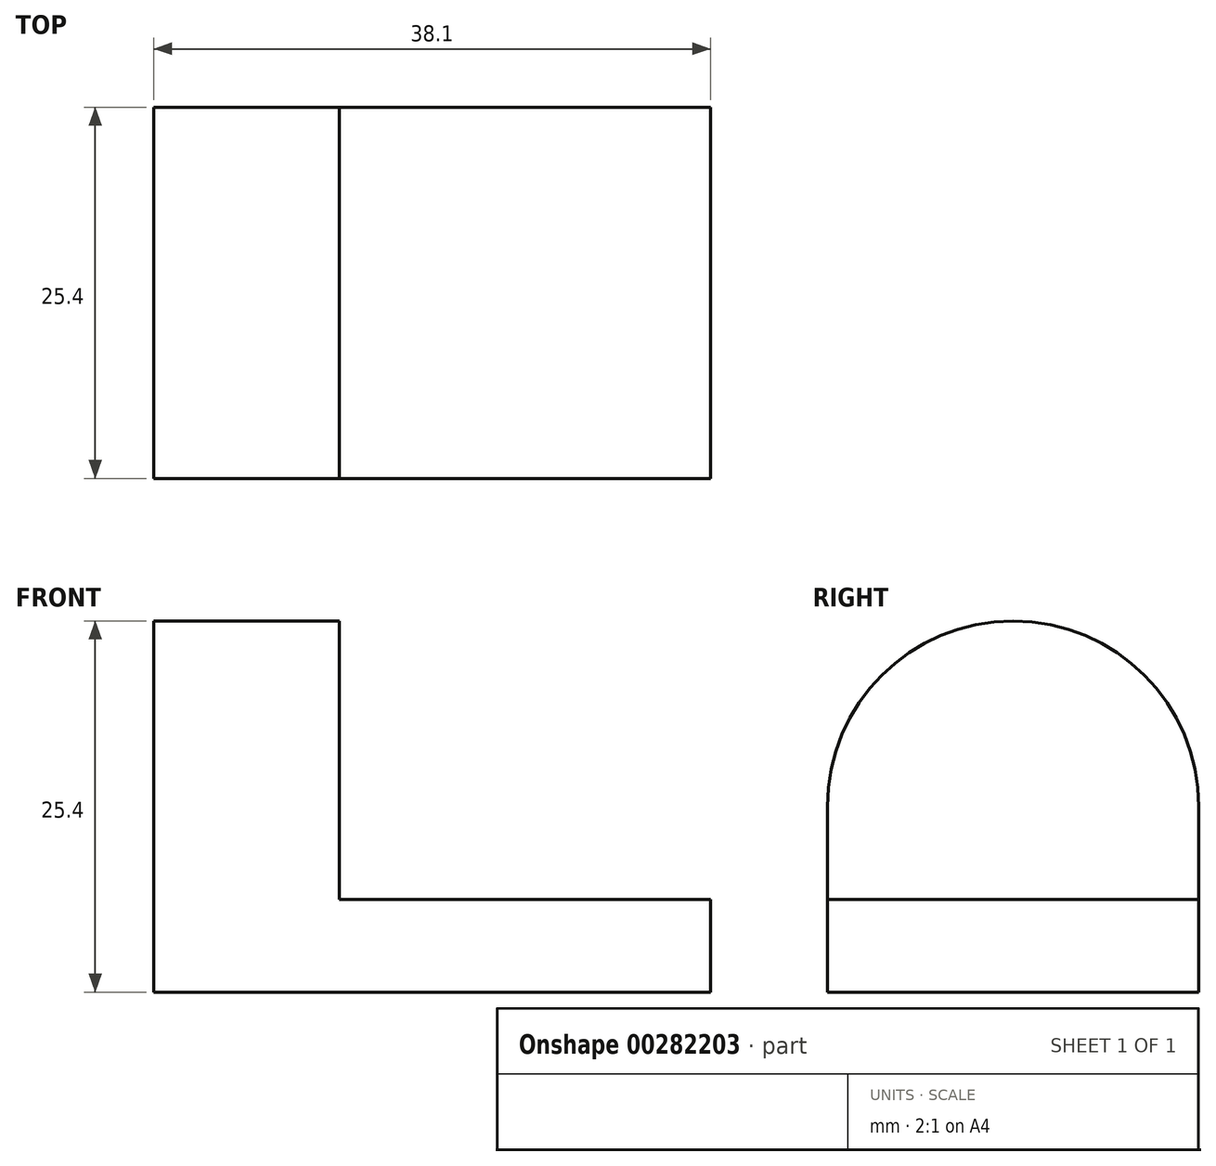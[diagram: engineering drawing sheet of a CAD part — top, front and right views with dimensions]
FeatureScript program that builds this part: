
annotation { "Feature Type Name" : "Feature", "Feature Type Description" : "" }
export const myFeature = defineFeature(function(context is Context, id is Id, definition is map)
    precondition{}
    {
        {
            var Q0;
            Q0=qCreatedBy(makeId("Right.planeOp"),FACE);
            var sketch = newSketch(context, id + "F0", { "sketchPlane" : qUnion([Q0])});
            skLineSegment(sketch, "E0.bottom", {"start": v(0, 0) * mm, "end": v(25.4, 0) * mm});
            skLineSegment(sketch, "E0.top", {"start": v(0, 6.35) * mm, "end": v(25.4, 6.35) * mm});
            skLineSegment(sketch, "E0.left", {"start": v(0, 0) * mm, "end": v(0, 6.35) * mm});
            skLineSegment(sketch, "E0.right", {"start": v(25.4, 0) * mm, "end": v(25.4, 6.35) * mm});
            skSolve(sketch);
        }
        {
            var Q0;
            Q0 = qSketchRegion(id + "F0", true);
            extrude(context, id + "F1", {"entities" : qUnion([Q0]), "depth" : 38.1 * mm});
        }
        {
            var Q0;
            Q0=qCreatedBy(makeId("Right.planeOp"),FACE);
            var sketch = newSketch(context, id + "F2", { "sketchPlane" : qUnion([Q0])});
            skLineSegment(sketch, "E1.bottom", {"start": v(25.4, 6.35) * mm, "end": v(0, 6.35) * mm});
            skLineSegment(sketch, "E1.top", {"start": v(25.4, 12.7) * mm, "end": v(0, 12.7) * mm});
            skLineSegment(sketch, "E1.left", {"start": v(25.4, 6.35) * mm, "end": v(25.4, 12.7) * mm});
            skLineSegment(sketch, "E1.right", {"start": v(0, 6.35) * mm, "end": v(0, 12.7) * mm});
            skSolve(sketch);
        }
        {
            var Q0;
            Q0 = qSketchRegion(id + "F2", true);
            extrude(context, id + "F3", {"entities" : qUnion([Q0]), "operationType" : NewBodyOperationType.ADD, "depth" : 12.7 * mm});
        }
        {
            var Q0;
            Q0=qCreatedBy(makeId("Right.planeOp"),FACE);
            var sketch = newSketch(context, id + "F4", { "sketchPlane" : qUnion([Q0])});
            skArc(sketch, "E2", {"start": v(25.4, 12.7) * mm, "mid": v(12.7, 25.4) * mm, "end": v(0, 12.7) * mm});
            skLineSegment(sketch, "E3", {"start": v(25.4, 12.7) * mm, "end": v(0, 12.7) * mm});
            skSolve(sketch);
        }
        {
            var Q0;
            Q0 = qSketchRegion(id + "F4", true);
            extrude(context, id + "F5", {"entities" : qUnion([Q0]), "operationType" : NewBodyOperationType.ADD, "depth" : 12.7 * mm});
        }
    });
